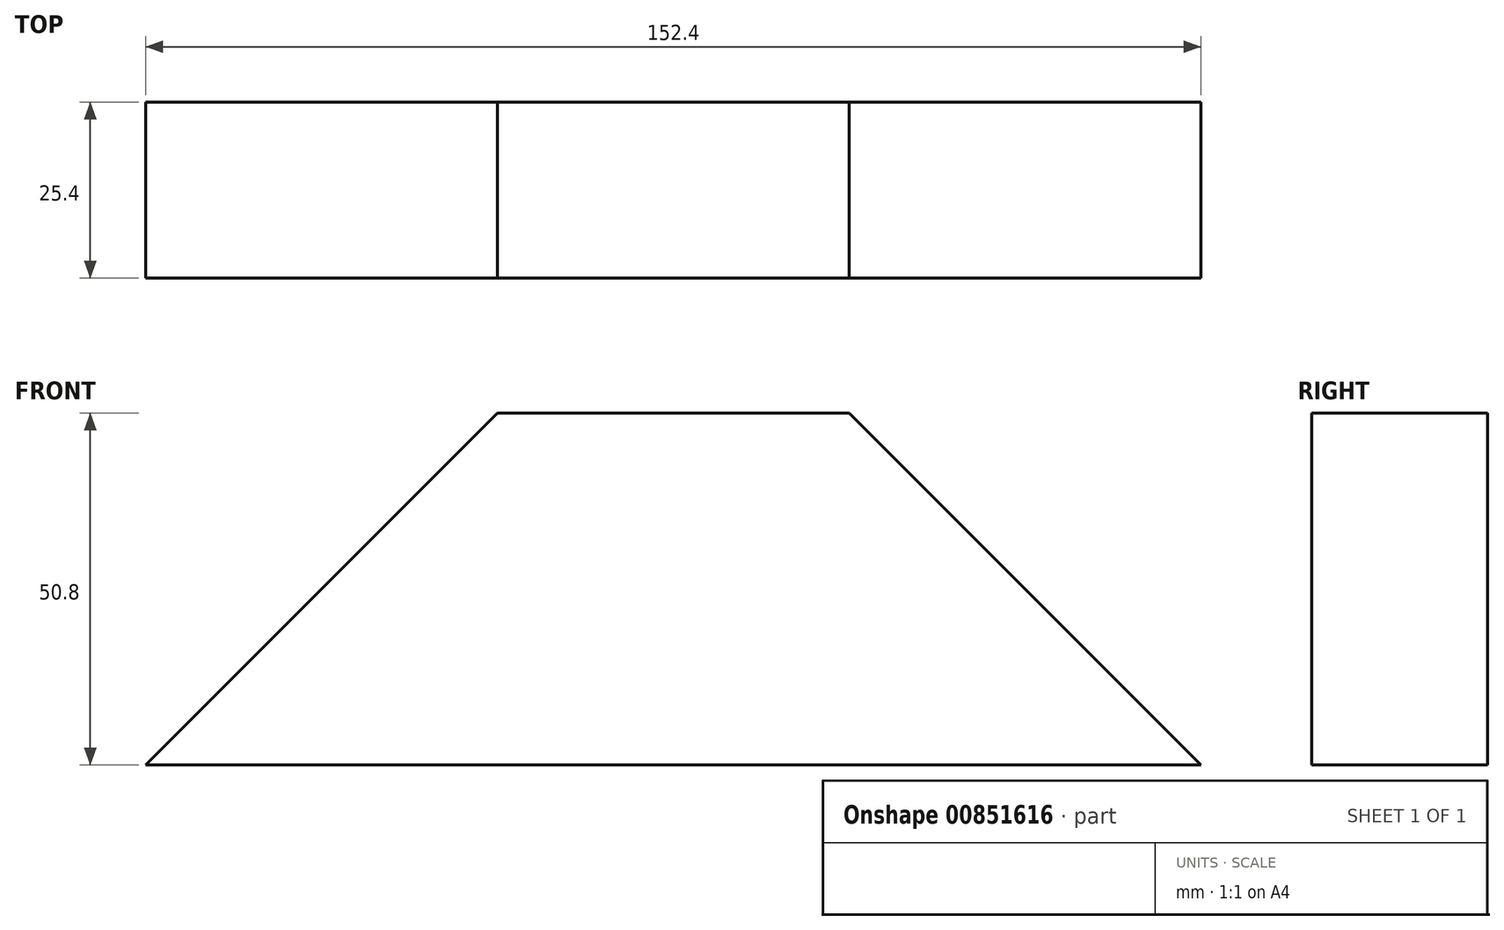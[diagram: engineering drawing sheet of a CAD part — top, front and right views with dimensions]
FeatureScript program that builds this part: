
annotation { "Feature Type Name" : "Feature", "Feature Type Description" : "" }
export const myFeature = defineFeature(function(context is Context, id is Id, definition is map)
    precondition{}
    {
        {
            var Q0;
            Q0=qCreatedBy(makeId("Front.planeOp"),FACE);
            var sketch = newSketch(context, id + "F0", { "sketchPlane" : qUnion([Q0])});
            skLineSegment(sketch, "E0", {"start": v(-64.1, -53.38) * mm, "end": v(88.3, -53.38) * mm});
            skLineSegment(sketch, "E1", {"start": v(-13.3, -2.58) * mm, "end": v(37.5, -2.58) * mm});
            skLineSegment(sketch, "E2", {"start": v(-13.3, -2.58) * mm, "end": v(-64.1, -53.38) * mm});
            skLineSegment(sketch, "E3", {"start": v(88.3, -53.38) * mm, "end": v(37.5, -2.58) * mm});
            skSolve(sketch);
        }
        {
            var Q0;
            Q0 = qSketchRegion(id + "F0", true);
            extrude(context, id + "F1", {"entities" : qUnion([Q0]), "depth" : 25.4 * mm, "offsetDistance" : 25.4 * mm});
        }
    });
